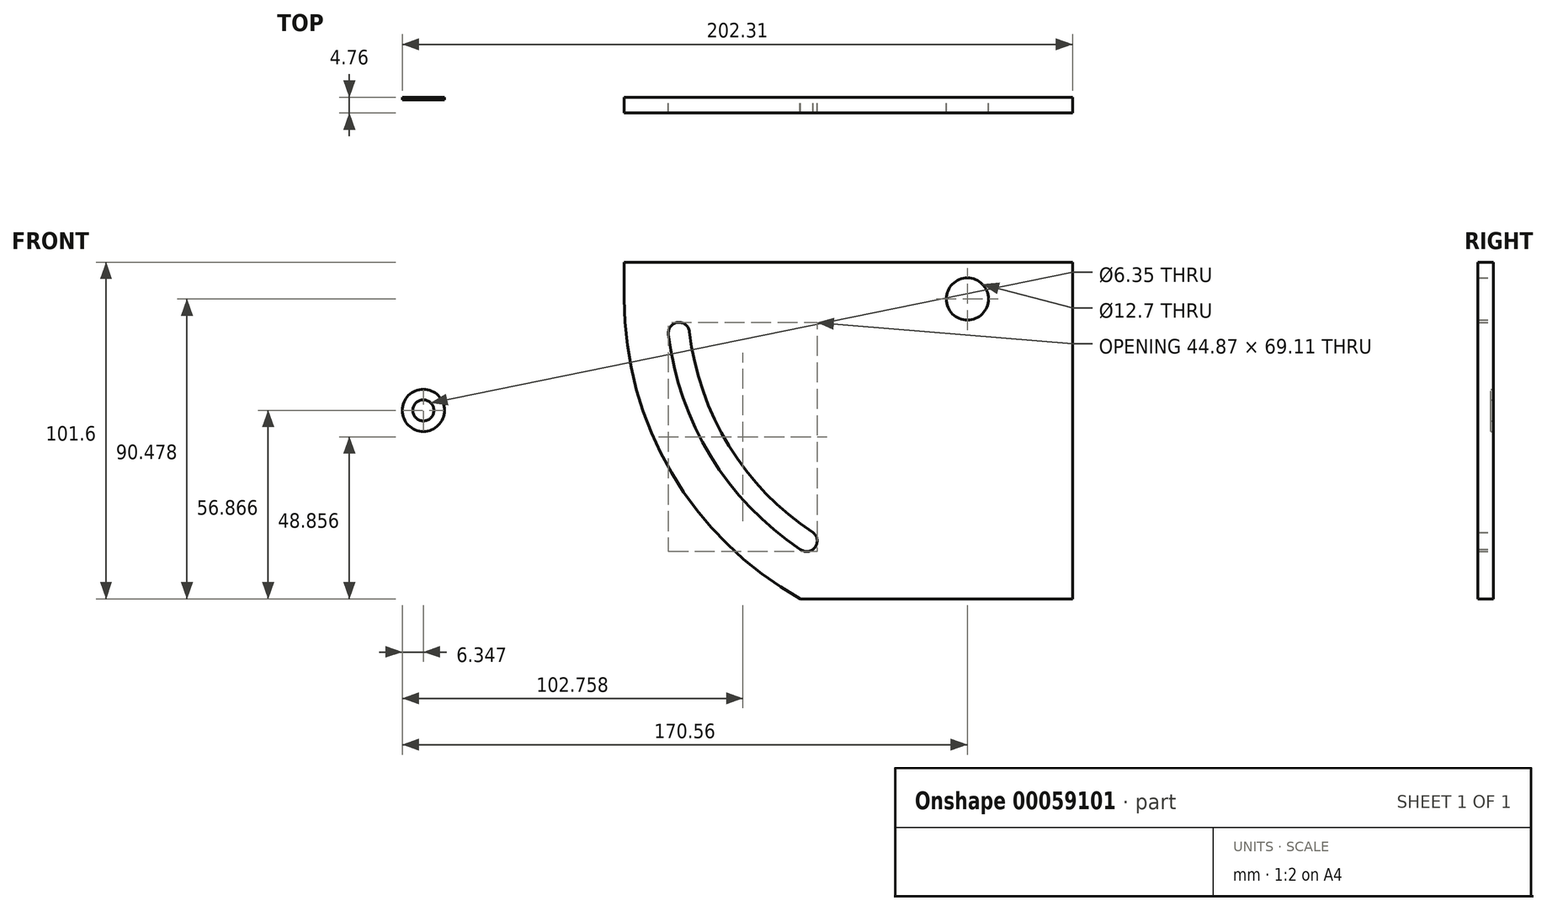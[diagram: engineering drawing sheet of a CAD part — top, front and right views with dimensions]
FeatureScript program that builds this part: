
annotation { "Feature Type Name" : "Feature", "Feature Type Description" : "" }
export const myFeature = defineFeature(function(context is Context, id is Id, definition is map)
    precondition{}
    {
        {
            var Q0;
            Q0=qCreatedBy(makeId("Front.planeOp"),FACE);
            var sketch = newSketch(context, id + "F0", { "sketchPlane" : qUnion([Q0])});
            skLineSegment(sketch, "E0.rect.bottom", {"start": v(79.47, -43.65) * mm, "end": v(-2.66, -43.65) * mm});
            skLineSegment(sketch, "E0.rect.top", {"start": v(79.47, 57.95) * mm, "end": v(-55.84, 57.95) * mm});
            skLineSegment(sketch, "E0.rect.right", {"start": v(-55.84, 46.83) * mm, "end": v(-55.84, 46.83) * mm});
            skLineSegment(sketch, "E1", {"start": v(-55.84, 46.83) * mm, "end": v(79.47, 46.83) * mm, "construction": true});
            skLineSegment(sketch, "E2", {"start": v(79.47, 57.95) * mm, "end": v(79.47, -43.65) * mm});
            skLineSegment(sketch, "E3", {"start": v(47.72, 57.95) * mm, "end": v(47.72, -43.65) * mm, "construction": true});
            skCircle(sketch, "E4", {"center": v(47.72, 46.83) * mm, "radius": 6.35 * mm});
            skArc(sketch, "E5", {"start": v(-42.52, 36.23) * mm, "mid": v(-29.78, -0.6) * mm, "end": v(-2.79, -28.7) * mm});
            skLineSegment(sketch, "E6", {"start": v(-42.86, 39.76) * mm, "end": v(-42.85, 39.76) * mm});
            skLineSegment(sketch, "E7.trimOffspring", {"start": v(-36.5, 39.76) * mm, "end": v(-36.49, 39.76) * mm});
            skLineSegment(sketch, "E8", {"start": v(1.17, -23.68) * mm, "end": v(1.16, -23.7) * mm});
            skArc(sketch, "E9", {"start": v(-2.78, -28.69) * mm, "mid": v(1.7, -28.16) * mm, "end": v(1.16, -23.7) * mm});
            skLineSegment(sketch, "E10.trimOffspring", {"start": v(-2.78, -28.69) * mm, "end": v(-2.79, -28.7) * mm});
            skLineSegment(sketch, "E11", {"start": v(47.72, 46.83) * mm, "end": v(-55.13, 34.75) * mm, "construction": true});
            skArc(sketch, "E12.trimOffspring", {"start": v(-36.19, 36.97) * mm, "mid": v(-24.21, 2.52) * mm, "end": v(1.17, -23.68) * mm});
            skArc(sketch, "E13", {"start": v(-36.19, 36.97) * mm, "mid": v(-39.72, 39.76) * mm, "end": v(-42.52, 36.23) * mm});
            skArc(sketch, "E14", {"start": v(-55.84, 46.83) * mm, "mid": v(-41.56, -5.64) * mm, "end": v(-2.66, -43.65) * mm});
            skLineSegment(sketch, "E15", {"start": v(-55.84, 57.95) * mm, "end": v(-55.84, 46.83) * mm});
            skSolve(sketch);
        }
        {
            var Q0;
            Q0=makeQuery(id+"F0.imprint","IMPRINT",FACE,{"disambiguationData":[TD([[makeQuery(id+"F0.imprint","IMPRINT",EDGE,{"derivedFrom":sQuery(id+"F0.wireOp",EDGE,"E0.rect.bottom")}),-1.0]])]});
            extrude(context, id + "F1", {"entities" : qUnion([Q0]), "depth" : 4.76 * mm});
        }
        {
            var Q0;
            Q0=qCreatedBy(makeId("Front.planeOp"),FACE);
            var sketch = newSketch(context, id + "F2", { "sketchPlane" : qUnion([Q0])});
            skCircle(sketch, "E16", {"center": v(-116.5, 13.22) * mm, "radius": 3.17 * mm});
            skCircle(sketch, "E17", {"center": v(-116.5, 13.22) * mm, "radius": 6.35 * mm});
            skSolve(sketch);
        }
        {
            var Q0;
            Q0=makeQuery(id+"F2.imprint","IMPRINT",FACE,{"disambiguationData":[TD([[makeQuery(id+"F2.imprint","IMPRINT",EDGE,{"derivedFrom":sQuery(id+"F2.wireOp",EDGE,"E16")}),-1.0]])]});
            extrude(context, id + "F3", {"entities" : qUnion([Q0]), "depth" : 0.79 * mm});
        }
    });
